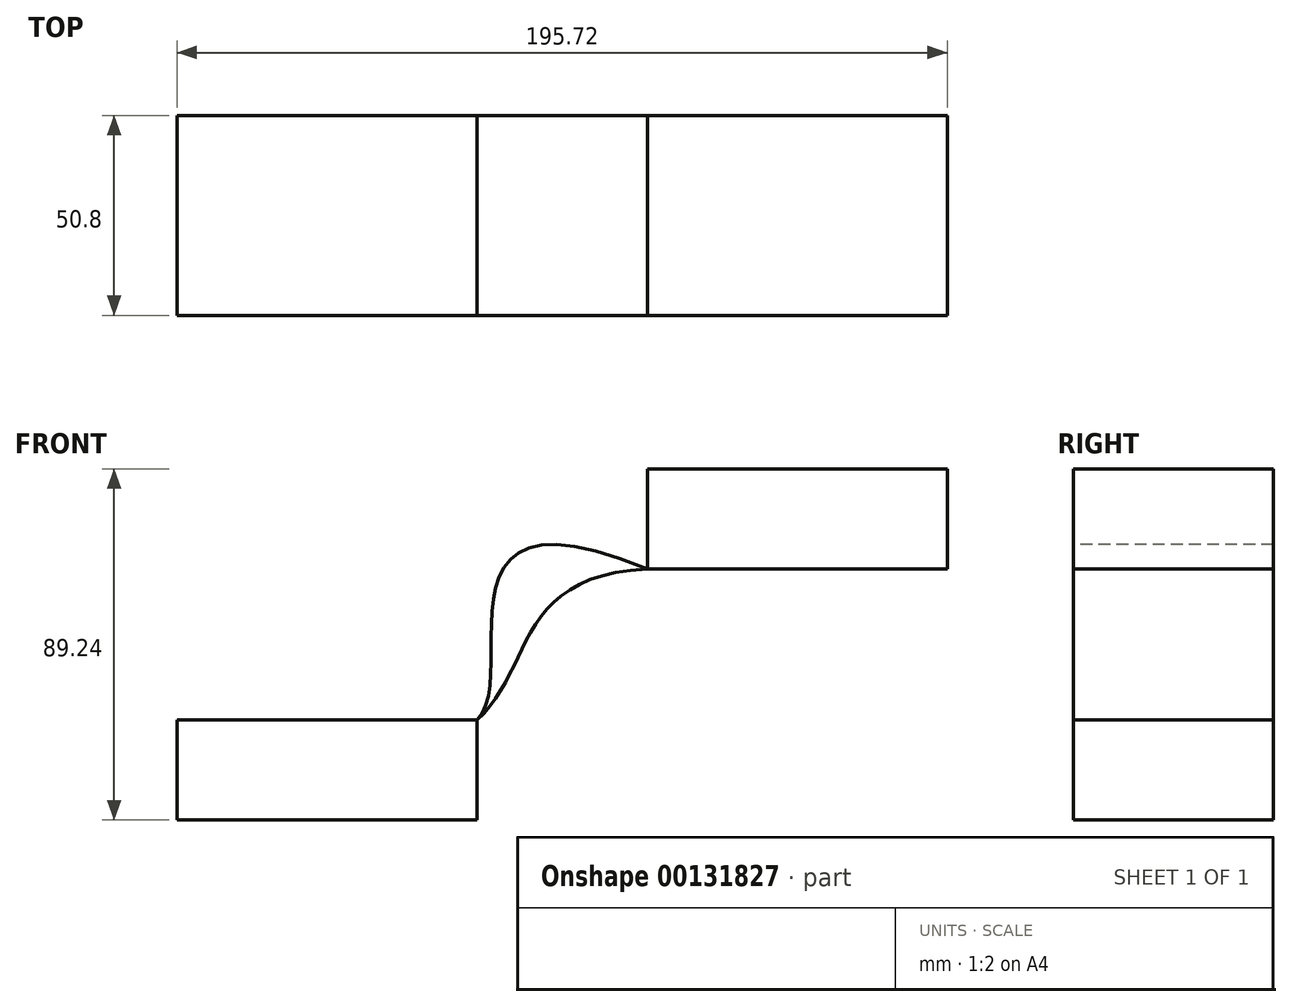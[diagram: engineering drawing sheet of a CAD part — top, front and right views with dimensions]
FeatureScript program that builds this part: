
annotation { "Feature Type Name" : "Feature", "Feature Type Description" : "" }
export const myFeature = defineFeature(function(context is Context, id is Id, definition is map)
    precondition{}
    {
        {
            var Q0;
            Q0=qCreatedBy(makeId("Front.planeOp"),FACE);
            var sketch = newSketch(context, id + "F0", { "sketchPlane" : qUnion([Q0])});
            skLineSegment(sketch, "E0.bottom", {"start": v(-13.69, -40.98) * mm, "end": v(-89.89, -40.98) * mm});
            skLineSegment(sketch, "E0.top", {"start": v(-13.69, -15.58) * mm, "end": v(-89.89, -15.58) * mm});
            skLineSegment(sketch, "E0.left", {"start": v(-13.69, -40.98) * mm, "end": v(-13.69, -15.58) * mm});
            skLineSegment(sketch, "E0.right", {"start": v(-89.89, -40.98) * mm, "end": v(-89.89, -15.58) * mm});
            skPoint(sketch, "E0.middle", {"position": v(-51.79, -28.28) * mm});
            skLineSegment(sketch, "E1.bottom", {"start": v(105.83, 22.86) * mm, "end": v(29.63, 22.86) * mm});
            skLineSegment(sketch, "E1.top", {"start": v(105.83, 48.26) * mm, "end": v(29.63, 48.26) * mm});
            skLineSegment(sketch, "E1.left", {"start": v(105.83, 22.86) * mm, "end": v(105.83, 48.26) * mm});
            skLineSegment(sketch, "E1.right", {"start": v(29.63, 22.86) * mm, "end": v(29.63, 48.26) * mm});
            skPoint(sketch, "E1.middle", {"position": v(67.73, 35.56) * mm});
            skFitSpline(sketch, "E2", {"points": [v(-13.69, -15.58) * mm, v(29.63, 22.86) * mm], "startDerivative": vector(34.8, 33.02) * mm, "endDerivative": vector(172.37, -70.9) * mm});
            skFitSpline(sketch, "E3", {"points": [v(-13.69, -15.58) * mm, v(29.63, 22.86) * mm], "startDerivative": vector(43.32, 38.44) * mm, "endDerivative": vector(102.44, 5.38) * mm});
            skSolve(sketch);
        }
        {
            var Q0;
            Q0 = qSketchRegion(id + "F0", true);
            extrude(context, id + "F1", {"entities" : qUnion([Q0]), "endBound" : BoundingType.SYMMETRIC, "depth" : 50.8 * mm});
        }
    });
